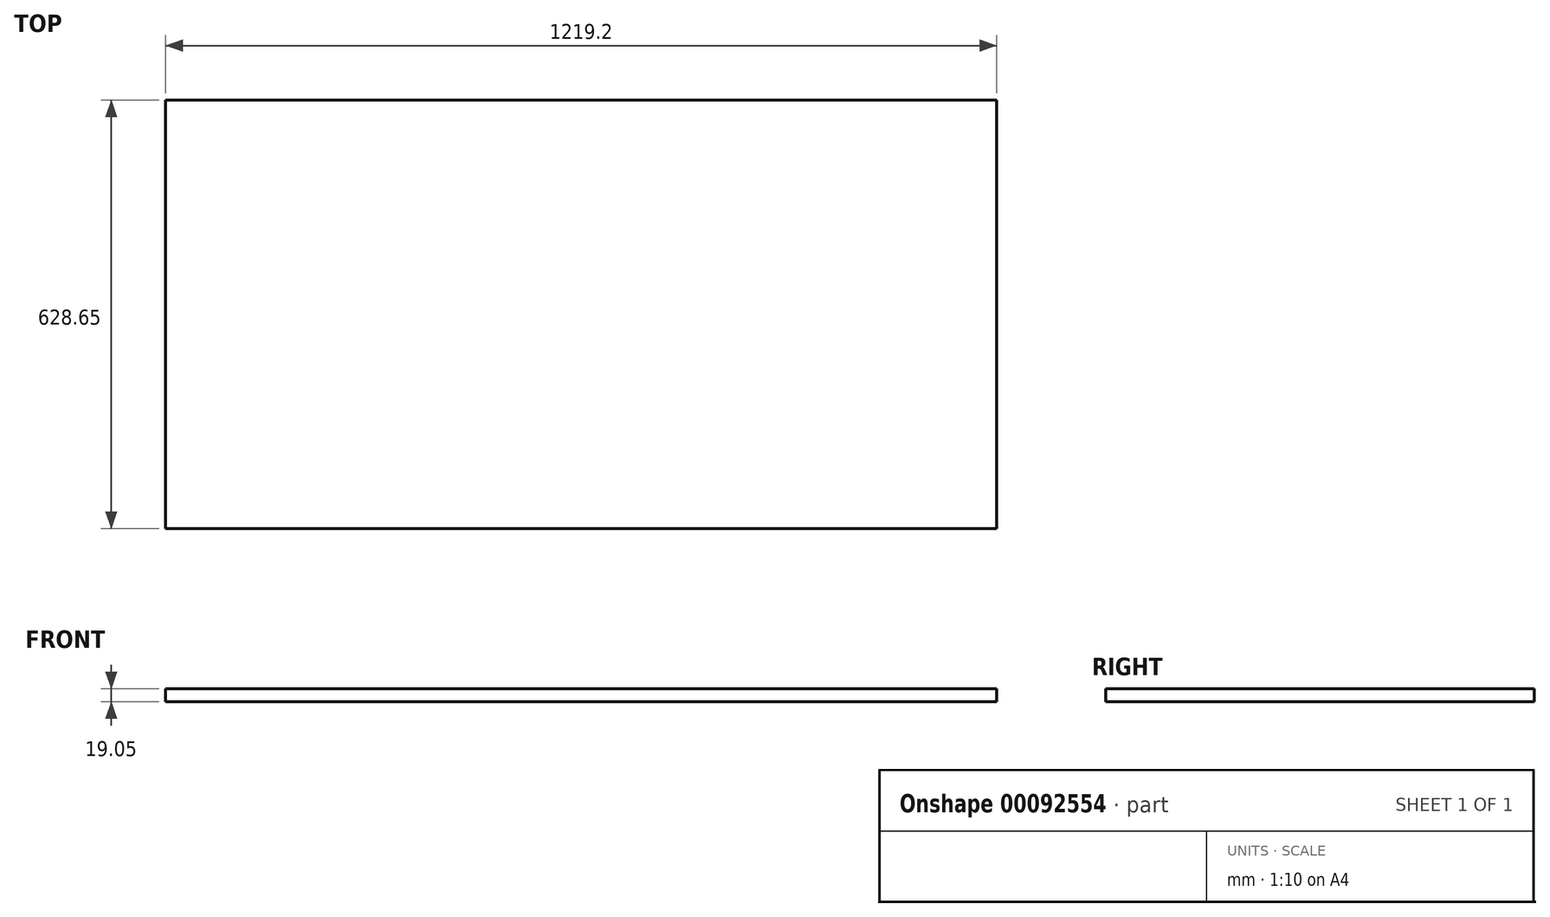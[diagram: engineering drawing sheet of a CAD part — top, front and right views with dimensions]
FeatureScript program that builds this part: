
annotation { "Feature Type Name" : "Feature", "Feature Type Description" : "" }
export const myFeature = defineFeature(function(context is Context, id is Id, definition is map)
    precondition{}
    {
        {
            var Q0;
            Q0=qCreatedBy(makeId("Front.planeOp"),FACE);
            var sketch = newSketch(context, id + "F0", { "sketchPlane" : qUnion([Q0])});
            skLineSegment(sketch, "E0.bottom", {"start": v(-624.26, 19.05) * mm, "end": v(594.94, 19.05) * mm});
            skLineSegment(sketch, "E0.top", {"start": v(-624.26, 0) * mm, "end": v(594.94, 0) * mm});
            skLineSegment(sketch, "E0.left", {"start": v(-624.26, 19.05) * mm, "end": v(-624.26, 0) * mm});
            skLineSegment(sketch, "E0.right", {"start": v(594.94, 19.05) * mm, "end": v(594.94, 0) * mm});
            skSolve(sketch);
        }
        {
            var Q0;
            Q0=makeQuery(id+"F0.imprint","IMPRINT",FACE,{"disambiguationData":[TD([[makeQuery(id+"F0.imprint","IMPRINT",EDGE,{"derivedFrom":sQuery(id+"F0.wireOp",EDGE,"E0.bottom")}),-1.0]])]});
            extrude(context, id + "F1", {"entities" : qUnion([Q0]), "depth" : 628.65 * mm});
        }
    });
